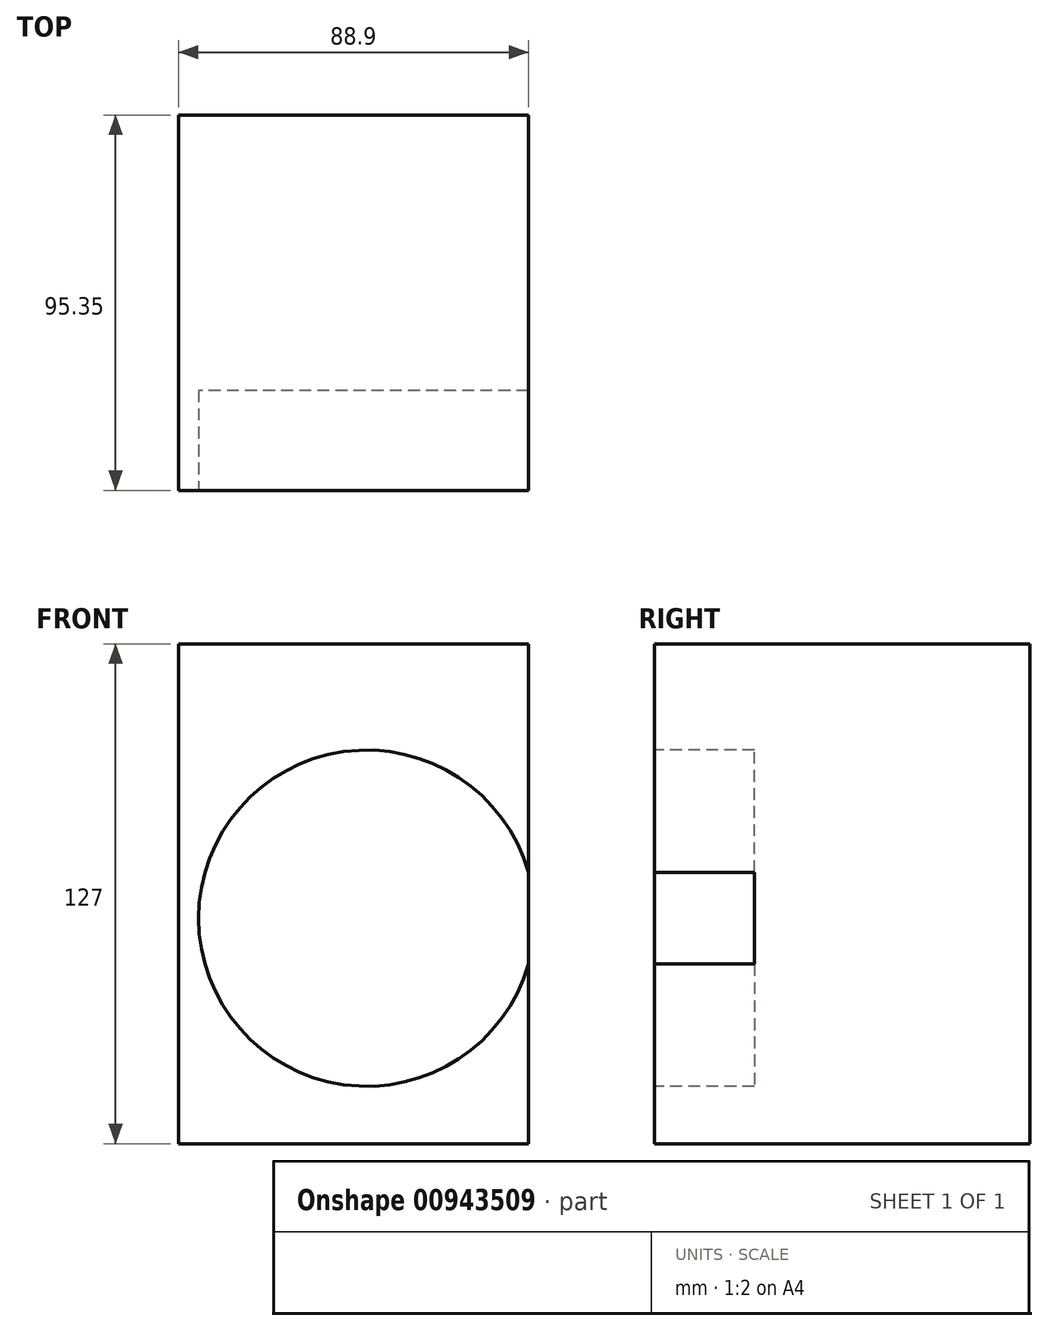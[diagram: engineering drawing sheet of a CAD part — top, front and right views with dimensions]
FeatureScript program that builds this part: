
annotation { "Feature Type Name" : "Feature", "Feature Type Description" : "" }
export const myFeature = defineFeature(function(context is Context, id is Id, definition is map)
    precondition{}
    {
        {
            var Q0;
            Q0=qCreatedBy(makeId("Top.planeOp"),FACE);
            var sketch = newSketch(context, id + "F0", { "sketchPlane" : qUnion([Q0])});
            skLineSegment(sketch, "E0.bottom", {"start": v(27.03, -43.48) * mm, "end": v(-61.87, -43.48) * mm});
            skLineSegment(sketch, "E0.top", {"start": v(27.03, 51.87) * mm, "end": v(-61.87, 51.87) * mm});
            skLineSegment(sketch, "E0.left", {"start": v(27.03, -43.48) * mm, "end": v(27.03, 51.87) * mm});
            skLineSegment(sketch, "E0.right", {"start": v(-61.87, -43.48) * mm, "end": v(-61.87, 51.87) * mm});
            skSolve(sketch);
        }
        {
            var Q0;
            Q0=makeQuery(id+"F0.imprint","IMPRINT",FACE,{"disambiguationData":[TD([[makeQuery(id+"F0.imprint","IMPRINT",EDGE,{"derivedFrom":sQuery(id+"F0.wireOp",EDGE,"E0.bottom")}),-1.0]])]});
            extrude(context, id + "F1", {"entities" : qUnion([Q0]), "depth" : 127 * mm, "offsetDistance" : 25.4 * mm});
        }
        {
            var Q0;
            Q0=makeQuery(id+"F1.opExtrude","SWEPT_FACE",FACE,{"disambiguationData":[OSD([sQuery(id+"F0.wireOp",EDGE,"E0.bottom")])]});
            var sketch = newSketch(context, id + "F2", { "sketchPlane" : qUnion([Q0])});
            skCircle(sketch, "E1", {"center": v(-14.05, 57.29) * mm, "radius": 42.7 * mm});
            skSolve(sketch);
        }
        {
            var Q0;
            {var subQ0=sQuery(id+"F2.wireOp",EDGE,"E1");var subQ1=makeQuery(id+"F1.opExtrude","SWEPT_EDGE",EDGE,{"disambiguationData":[OSD([sQuery(id+"F0.wireOp",EDGE,"E0.bottom"),sQuery(id+"F0.wireOp",EDGE,"E0.left")])]});var subQ2=makeQuery(id+"F2.imprint","INTERSECT",VERTEX,{"disambiguationData":[OD(0.0)],"derivedFrom":[subQ1,subQ0]});Q0=makeQuery(id+"F2.imprint","IMPRINT",FACE,{"disambiguationData":[TD([[makeQuery(id+"F2.imprint","IMPRINT",EDGE,{"disambiguationData":[TD([[subQ2,-1.0]])],"derivedFrom":subQ0}),1.0]])]});}
            var Q1;
            {var subQ0=sQuery(id+"F2.wireOp",EDGE,"E1");var subQ1=makeQuery(id+"F1.opExtrude","SWEPT_EDGE",EDGE,{"disambiguationData":[OSD([sQuery(id+"F0.wireOp",EDGE,"E0.bottom"),sQuery(id+"F0.wireOp",EDGE,"E0.left")])]});var subQ2=makeQuery(id+"F2.imprint","INTERSECT",VERTEX,{"disambiguationData":[OD(0.0)],"derivedFrom":[subQ1,subQ0]});Q1=makeQuery(id+"F2.imprint","IMPRINT",FACE,{"disambiguationData":[TD([[makeQuery(id+"F2.imprint","IMPRINT",EDGE,{"disambiguationData":[TD([[subQ2,1.0]])],"derivedFrom":subQ0}),1.0]])]});}
            extrude(context, id + "F3", {"entities" : qUnion([Q0, Q1]), "operationType" : NewBodyOperationType.REMOVE, "oppositeDirection" : true, "depth" : 25.4 * mm, "offsetDistance" : 25.4 * mm});
        }
    });
